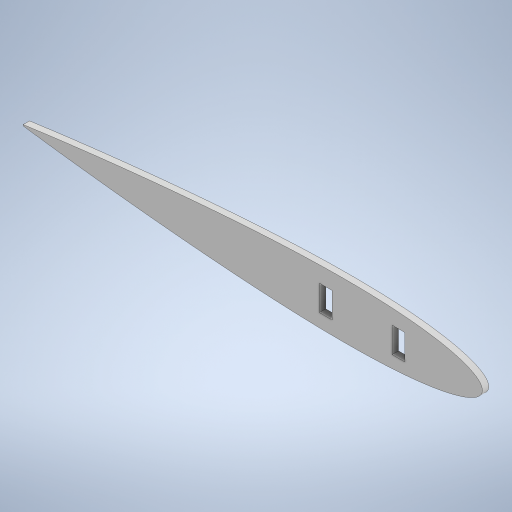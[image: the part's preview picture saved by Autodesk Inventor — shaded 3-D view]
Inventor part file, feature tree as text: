
AUTODESK INVENTOR PART (.ipt)
format: ipt  version: 2024 (Build 280153000, 153)  size: 287,232 bytes
history: native  units: in
note: dims shown in document units (in); Inventor stores cm internally (conversion verified against a paired STEP export)
features: projected_geometry x4, extrude x3, sketch x3
ambient origin geometry x8: Origin, YZ Plane, XZ Plane, XY Plane, X Axis, Y Axis, Z Axis, Center Point
bodies: Solid1 (feature_tree)
feature tree (10):
  extrude  "Extrusion1"  Depth=0.3937in TaperAngle=0.0deg
  extrude  "Extrusion2"  [1 undecoded]
  extrude  "Extrusion3"  [1 undecoded]
  sketch  "Sketch1"  dims[d0=0.0984in d1=0.0in d2=0.3937in d3=0.0in]
  sketch  "Sketch3"  dims[d5=0.0984in d6=0.0in]
  projected_geometry  "Projected Loop2"
  projected_geometry  "Projected Loop3"
  projected_geometry  "Projected Loop4"
  projected_geometry  "Projected Loop5"
  sketch  "Sketch4"
note: 2 required parameter values undecoded (feature->parameter linkage not recoverable at this tier; creation-order binding heuristic only, values carry confidence <= 0.55)
